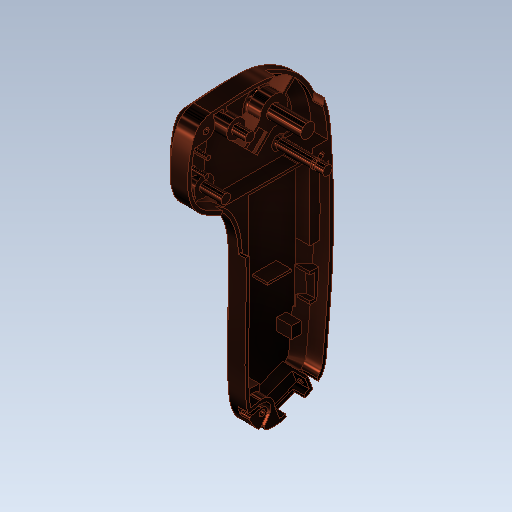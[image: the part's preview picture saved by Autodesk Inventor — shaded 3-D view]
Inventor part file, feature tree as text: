
AUTODESK INVENTOR PART (.ipt)
format: ipt  version: 2020.1 (Build 241239000, 239)  size: 1,645,056 bytes
history: native  units: mm
features: extrude x20, reference x20, sketch x16, other x15, plane x8, fillet x4, chamfer x3, projected_geometry x2, shell x1, draft x1, mirror x1, emboss x1, loft x1, revolve x1
ambient origin geometry x8: Origin, YZ Plane, XZ Plane, XY Plane, X Axis, Y Axis, Z Axis, Center Point
bodies: Body1 (feature_tree), Body2 (feature_tree)
feature tree (94):
  other  "Remote Bottom Shell"
  other  "Outline"
  other  "Acceleration Knob"
  extrude  "Extrusion1"  Depth=33.5mm
  chamfer  "Chamfer1"  Distance=200.0mm Angle=360.0deg
  shell  "Shell1"  Thickness=12.0mm
  extrude  "Extrusion2"  Depth=1.5mm
  sketch  "Sketch8"  dims[d0=131.0mm d86=33.5mm]
  extrude  "Extrusion5"  Depth=4.2mm TaperAngle=0.0deg
  extrude  "Extrusion6"  Depth=12.0mm
  plane  "Work Plane3"
  extrude  "Extrusion7"  Depth=5.0mm
  sketch  "Sketch10"  dims[d96=4.6mm d97=2.0mm d98=45.0deg d99=1.5mm]
  extrude  "Extrusion8"  Depth=6.5mm
  extrude  "Extrusion9"  Depth=4.0mm
  plane  "Work Plane4"
  sketch  "Sketch11"  dims[d103=0.35mm d104=4.2mm d105=0.0mm]
  extrude  "Extrusion10"  Depth=1.5mm
  extrude  "Extrusion11"  Depth=1.5mm
  plane  "Work Plane5"
  extrude  "Extrusion12"  Depth=2.5mm
  extrude  "Extrusion13"  Depth=4.0mm
  extrude  "Extrusion14"  Depth=4.0mm
  extrude  "Extrusion15"  Depth=1.5mm
  chamfer  "Chamfer3"  Angle=45.0deg  [1 undecoded]
  plane  "Work Plane6"
  extrude  "Extrusion16"  Depth=2.0mm
  draft  "FaceDraft1"
  extrude  "Extrusion17"  Depth=4.0mm
  fillet  "Fillet1"  Radius=1.0mm
  sketch  "Sketch17"  dims[d129=8.0mm d130=1.5mm]
  plane  "Work Plane7"
  extrude  "Extrusion18"  Depth=1.0mm
  plane  "Work Plane8"
  mirror  "Mirror1"
  extrude  "Extrusion20"  Depth=4.5mm
  emboss  "Emboss1"
  plane  "Work Plane9"
  extrude  "Extrusion21"  TaperAngle=45.0deg  [1 undecoded]
  extrude  "Extrusion22"  Depth=1.5mm
  chamfer  "Chamfer4"  Distance=1.5mm
  loft  "Loft1"
  fillet  "Fillet2"  Radius=82.0mm
  fillet  "Fillet3"  Radius=4.623mm
  plane  "Work Plane10"
  revolve  "Revolution1"  [1 undecoded]
  fillet  "Fillet4"  Radius=20.2mm
  extrude  "Extrusion23"  Depth=4.0mm TaperAngle=0.0deg
  other  "Image1"
  sketch  "Sketch9"  dims[d87=31.0mm d88=200.0mm d90=360.0deg d94=12.0mm d95=0.0mm]
  sketch  "Sketch12"  dims[d121=6.0mm d122=12.0mm]
  sketch  "Sketch14"  dims[d123=8.0mm d124=5.0mm]
  sketch  "Sketch15"  dims[d125=7.5mm d126=6.5mm]
  sketch  "Sketch16"  dims[d127=45.0deg d128=4.0mm]
  reference  "Reference2"
  reference  "Reference3"
  reference  "Reference4"
  other  "Plate"
  other  "Plate Solid"
  sketch  "Sketch19"  dims[d131=1.5mm d134=1.5mm]
  sketch  "Sketch20"  dims[d135=3.5mm d136=2.5mm]
  reference  "Reference5"
  reference  "Reference6"
  reference  "Reference7"
  reference  "Reference8"
  reference  "Reference9"
  reference  "Reference10"
  reference  "Reference11"
  reference  "Reference12"
  reference  "Reference13"
  reference  "Reference14"
  reference  "Reference15"
  reference  "Reference16"
  sketch  "Sketch21"  dims[d137=1.0mm d138=4.0mm]
  sketch  "Sketch22"  dims[d140=45.0deg d141=4.0mm]
  sketch  "Sketch23"  dims[d142=8.5mm d143=1.5mm]
  projected_geometry  "Projected Loop1"
  other  "Work Axis1"
  sketch  "Sketch24"  dims[d144=1.0mm]
  projected_geometry  "Projected Loop2"
  sketch  "Sketch25"  dims[d145=2.0mm d146=45.0deg d147=2.0mm d148=4.0mm d150=1.0mm d151=1.0mm d152=4.5mm d153=45.0deg d156=1.5mm d157=1.5mm d159=25.0mm d160=82.0mm d161=4.623mm d163=4.0mm d164=20.2mm d165=0.0mm d166=4.0mm d167=0.0mm d168=20.7mm d169=4.0mm d170=0.0mm d171=4.0mm d172=0.0mm d173=1.0mm d174=0.0mm d175=-3.0mm d176=1.0mm d177=0.0mm d178=9.2mm d179=0.0mm d180=8.5mm d181=9.2mm d182=0.0mm d197=5.5mm d198=0.0mm d199=4.5mm d200=0.0mm d201=26.0mm d202=36.0mm d204=26.0mm d205=20.0mm d206=1.0mm d208=10.0mm d209=4.5mm d210=8.0mm d211=18.2mm d212=14.2mm d213=4.5mm d214=5.0mm d215=1.2mm d216=4.0mm d217=4.0mm d218=2.1mm d220=5.2mm d221=5.2mm d224=7.4mm d225=0.0mm d226=1.0mm d227=2.0mm d228=45.0deg d229=0.001mm d230=10.0mm d231=0.0mm d232=45.0deg d234=3.0mm d235=0.0mm d236=1.0mm d237=13.4mm d238=1.2mm d239=2.75mm d240=2.5mm d241=2.5mm d242=1.9mm d243=0.5mm d244=0.0mm d246=1.0mm d247=3.5mm d248=2.0mm d251=0.8mm d252=0.0mm d254=0.5mm d255=0.0mm d257=7.65mm d258=1.85mm d259=1.85mm d260=1.020476mm d261=1.020476mm d264=7.65mm d265=0.0mm d266=6.0mm d267=0.0mm d268=0.2mm d269=2.0mm d270=45.0deg d271=2.0mm d272=1.5mm d273=1.0mm d274=1.5mm d275=10.0mm d276=90.0deg d277=10.0mm d278=90.0deg d279=8.0mm d280=8.0mm d281=0.0mm d282=1.5mm d283=90.0deg d284=0.5mm d289=3.0mm d290=0.523599mm]
  reference  "Reference17"
  reference  "Reference18"
  reference  "Reference19"
  reference  "Reference20"
  reference  "Reference21"
  parser-record x1  (decoder bookkeeping rows leaked as tree rows — omitted from the tree; the rows remain in map.json)
  other  "Remote.iam"
  other  "Remote Top Shell:1"
  other  "SPDT Mini Slide Switch:1"
  other  "switch body 2_5431"
  other  "Microswitch Subminiature Lever SPDT Through Hole:1"
  other  "Lipo Charger - TP4056:1"
  other  "bOARD"
note: 3 required parameter values undecoded (feature->parameter linkage not recoverable at this tier; creation-order binding heuristic only, values carry confidence <= 0.55)
note: 1 file-system path scrubbed to <path> (originals preserved in map.json)